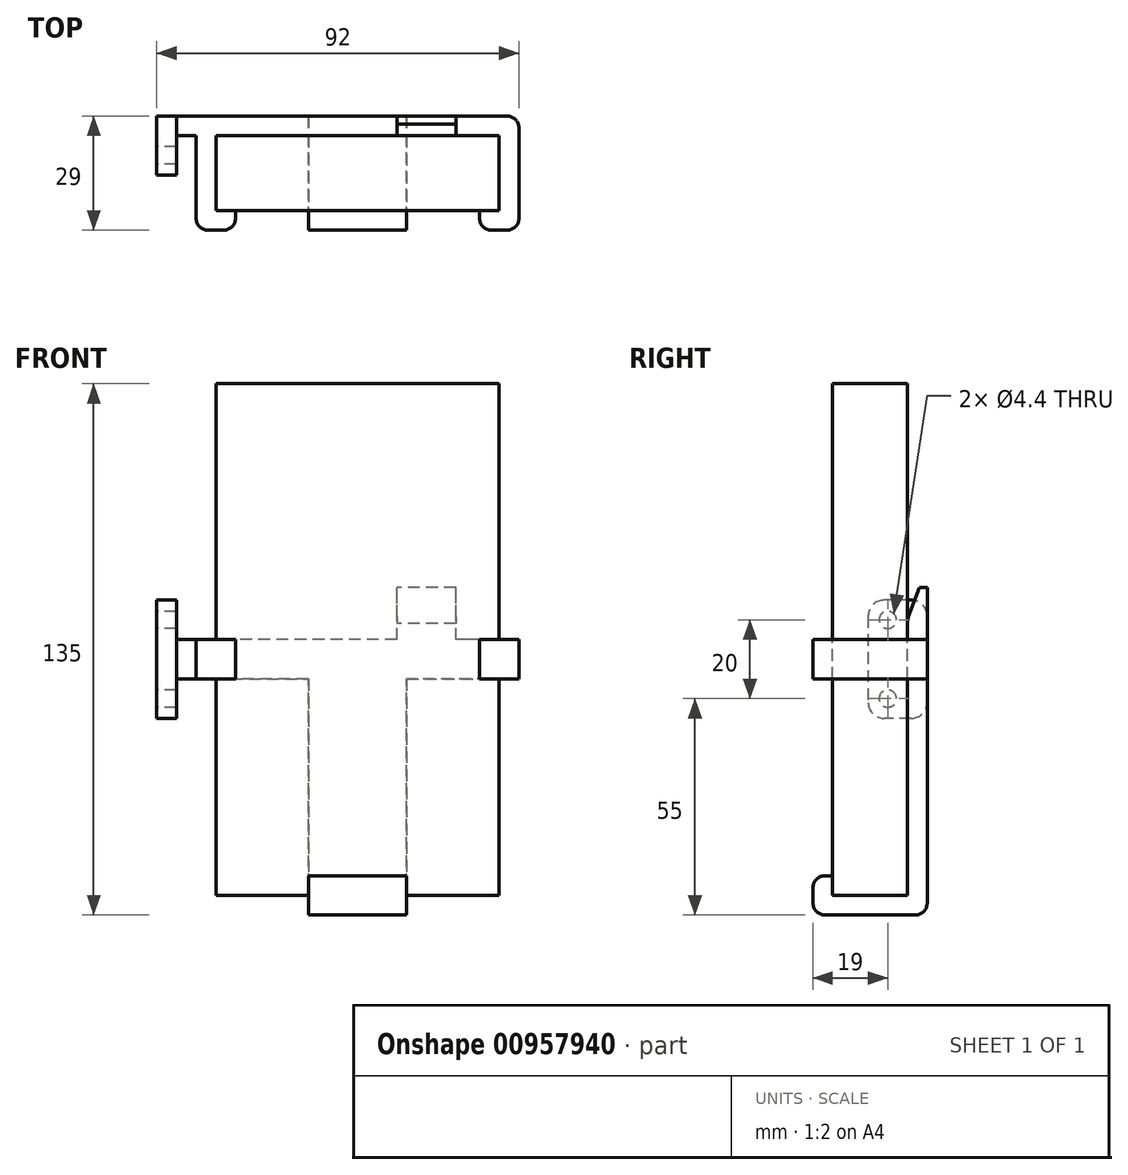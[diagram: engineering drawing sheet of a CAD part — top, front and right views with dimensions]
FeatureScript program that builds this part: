
annotation { "Feature Type Name" : "Feature", "Feature Type Description" : "" }
export const myFeature = defineFeature(function(context is Context, id is Id, definition is map)
    precondition{}
    {
        {
            var Q0;
            Q0=qCreatedBy(makeId("Front.planeOp"),FACE);
            var sketch = newSketch(context, id + "F0", { "sketchPlane" : qUnion([Q0])});
            skLineSegment(sketch, "E0.bottom", {"start": v(36, 65) * mm, "end": v(-36, 65) * mm});
            skLineSegment(sketch, "E0.top", {"start": v(36, -65) * mm, "end": v(-36, -65) * mm});
            skLineSegment(sketch, "E0.left", {"start": v(36, 65) * mm, "end": v(36, -65) * mm});
            skLineSegment(sketch, "E0.right", {"start": v(-36, 65) * mm, "end": v(-36, -65) * mm});
            skPoint(sketch, "E0.middle", {"position": v(0, 0) * mm});
            skSolve(sketch);
        }
        {
            var Q0;
            Q0=makeQuery(id+"F0.imprint","IMPRINT",FACE,{"disambiguationData":[TD([[makeQuery(id+"F0.imprint","IMPRINT",EDGE,{"derivedFrom":sQuery(id+"F0.wireOp",EDGE,"E0.bottom")}),1.0]])]});
            extrude(context, id + "F1", {"entities" : qUnion([Q0]), "depth" : 19 * mm, "offsetDistance" : 25 * mm});
        }
        {
            var Q0;
            Q0=qCreatedBy(makeId("Right.planeOp"),FACE);
            var sketch = newSketch(context, id + "F2", { "sketchPlane" : qUnion([Q0])});
            skLineSegment(sketch, "E1", {"start": v(0, 0) * mm, "end": v(0, -65) * mm});
            skLineSegment(sketch, "E2", {"start": v(0, -65) * mm, "end": v(-19, -65) * mm});
            skLineSegment(sketch, "E3", {"start": v(-19, -65) * mm, "end": v(-19, -60) * mm});
            skLineSegment(sketch, "E4", {"start": v(-19, -60) * mm, "end": v(-24, -60) * mm});
            skLineSegment(sketch, "E5", {"start": v(-24, -60) * mm, "end": v(-24, -70) * mm});
            skLineSegment(sketch, "E6", {"start": v(-24, -70) * mm, "end": v(5, -70) * mm});
            skLineSegment(sketch, "E7", {"start": v(5, -70) * mm, "end": v(5, 0) * mm});
            skLineSegment(sketch, "E8", {"start": v(5, 0) * mm, "end": v(0, 0) * mm});
            skLineSegment(sketch, "E9", {"start": v(0, -65) * mm, "end": v(0, 0) * mm});
            skSolve(sketch);
        }
        {
            var Q0;
            Q0=makeQuery(id+"F2.imprint","IMPRINT",FACE,{"disambiguationData":[TD([[makeQuery(id+"F2.imprint","IMPRINT",EDGE,{"derivedFrom":sQuery(id+"F2.wireOp",EDGE,"E2")}),1.0]])]});
            extrude(context, id + "F3", {"entities" : qUnion([Q0]), "endBound" : BoundingType.SYMMETRIC, "depth" : 25 * mm, "offsetDistance" : 25 * mm});
        }
        {
            var Q0;
            Q0=makeQuery(id+"F3.opExtrude","SWEPT_EDGE",EDGE,{"disambiguationData":[OSD([sQuery(id+"F2.wireOp",EDGE,"E4"),sQuery(id+"F2.wireOp",EDGE,"E5")])]});
            var Q1;
            Q1=makeQuery(id+"F3.opExtrude","SWEPT_EDGE",EDGE,{"disambiguationData":[OSD([sQuery(id+"F2.wireOp",EDGE,"E5"),sQuery(id+"F2.wireOp",EDGE,"E6")])]});
            var Q2;
            Q2=makeQuery(id+"F3.opExtrude","SWEPT_EDGE",EDGE,{"disambiguationData":[OSD([sQuery(id+"F2.wireOp",EDGE,"E6"),sQuery(id+"F2.wireOp",EDGE,"E7")])]});
            fillet(context, id + "F4", {"entities" : qUnion([Q0, Q1, Q2]), "radius" : 3 * mm, "tangentPropagation" : true, "allowEdgeOverflow" : false});
        }
        {
            var Q0;
            Q0=qCreatedBy(makeId("Top.planeOp"),FACE);
            var sketch = newSketch(context, id + "F5", { "sketchPlane" : qUnion([Q0])});
            skLineSegment(sketch, "E10", {"start": v(12.5, 0) * mm, "end": v(36, 0) * mm});
            skLineSegment(sketch, "E11", {"start": v(36, 0) * mm, "end": v(36, -19) * mm});
            skLineSegment(sketch, "E12", {"start": v(36, -19) * mm, "end": v(31, -19) * mm});
            skLineSegment(sketch, "E13", {"start": v(31, -19) * mm, "end": v(31, -24) * mm});
            skLineSegment(sketch, "E14", {"start": v(31, -24) * mm, "end": v(41, -24) * mm});
            skLineSegment(sketch, "E15", {"start": v(41, -24) * mm, "end": v(41, 5) * mm});
            skLineSegment(sketch, "E16", {"start": v(41, 5) * mm, "end": v(12.5, 5) * mm});
            skLineSegment(sketch, "E17", {"start": v(12.5, 5) * mm, "end": v(12.5, 0) * mm});
            skLineSegment(sketch, "E18.MirrorCS", {"start": v(-12.5, 5) * mm, "end": v(-12.5, 0) * mm});
            skLineSegment(sketch, "E19.MirrorCS", {"start": v(-12.5, 0) * mm, "end": v(-36, 0) * mm});
            skLineSegment(sketch, "E20.MirrorCS", {"start": v(-36, 0) * mm, "end": v(-36, -19) * mm});
            skLineSegment(sketch, "E21.MirrorCS", {"start": v(-36, -19) * mm, "end": v(-31, -19) * mm});
            skLineSegment(sketch, "E22.MirrorCS", {"start": v(-31, -19) * mm, "end": v(-31, -24) * mm});
            skLineSegment(sketch, "E23.MirrorCS", {"start": v(-31, -24) * mm, "end": v(-41, -24) * mm});
            skLineSegment(sketch, "E24.MirrorCS", {"start": v(-41, -24) * mm, "end": v(-41, 5) * mm});
            skLineSegment(sketch, "E25.MirrorCS", {"start": v(-41, 5) * mm, "end": v(-12.5, 5) * mm});
            skSolve(sketch);
        }
        {
            var Q0;
            Q0=makeQuery(id+"F5.imprint","IMPRINT",FACE,{"disambiguationData":[TD([[makeQuery(id+"F5.imprint","IMPRINT",EDGE,{"derivedFrom":sQuery(id+"F5.wireOp",EDGE,"E10")}),1.0]])]});
            var Q1;
            Q1=makeQuery(id+"F5.imprint","IMPRINT",FACE,{"disambiguationData":[TD([[makeQuery(id+"F5.imprint","IMPRINT",EDGE,{"derivedFrom":sQuery(id+"F5.wireOp",EDGE,"E18.MirrorCS")}),-1.0]])]});
            extrude(context, id + "F6", {"entities" : qUnion([Q0, Q1]), "operationType" : NewBodyOperationType.ADD, "oppositeDirection" : true, "depth" : 10 * mm, "offsetDistance" : 25 * mm});
        }
        {
            var Q0;
            Q0=makeQuery(id+"F6.opExtrude","SWEPT_EDGE",EDGE,{"disambiguationData":[OSD([sQuery(id+"F5.wireOp",EDGE,"E13"),sQuery(id+"F5.wireOp",EDGE,"E14")])]});
            var Q1;
            Q1=makeQuery(id+"F6.opExtrude","SWEPT_EDGE",EDGE,{"disambiguationData":[OSD([sQuery(id+"F5.wireOp",EDGE,"E14"),sQuery(id+"F5.wireOp",EDGE,"E15")])]});
            var Q2;
            Q2=makeQuery(id+"F6.opExtrude","SWEPT_EDGE",EDGE,{"disambiguationData":[OSD([sQuery(id+"F5.wireOp",EDGE,"E15"),sQuery(id+"F5.wireOp",EDGE,"E16")])]});
            var Q3;
            Q3=makeQuery(id+"F6.opExtrude","SWEPT_EDGE",EDGE,{"disambiguationData":[OSD([sQuery(id+"F5.wireOp",EDGE,"E23.MirrorCS"),sQuery(id+"F5.wireOp",EDGE,"E24.MirrorCS")])]});
            var Q4;
            Q4=makeQuery(id+"F6.opExtrude","SWEPT_EDGE",EDGE,{"disambiguationData":[OSD([sQuery(id+"F5.wireOp",EDGE,"E22.MirrorCS"),sQuery(id+"F5.wireOp",EDGE,"E23.MirrorCS")])]});
            fillet(context, id + "F7", {"entities" : qUnion([Q0, Q1, Q2, Q3, Q4]), "radius" : 3 * mm, "tangentPropagation" : true, "allowEdgeOverflow" : false});
        }
        {
            var Q0;
            Q0=qCreatedBy(makeId("Top.planeOp"),FACE);
            var sketch = newSketch(context, id + "F8", { "sketchPlane" : qUnion([Q0])});
            skPoint(sketch, "E26.0", {"position": v(-41, 5) * mm});
            skLineSegment(sketch, "E27.bottom", {"start": v(-41, 5) * mm, "end": v(-51, 5) * mm});
            skLineSegment(sketch, "E27.top", {"start": v(-41, 0) * mm, "end": v(-51, 0) * mm});
            skLineSegment(sketch, "E27.left", {"start": v(-41, 5) * mm, "end": v(-41, 0) * mm});
            skLineSegment(sketch, "E27.right", {"start": v(-51, 5) * mm, "end": v(-51, 0) * mm});
            skSolve(sketch);
        }
        {
            var Q0;
            Q0=makeQuery(id+"F8.imprint","IMPRINT",FACE,{"disambiguationData":[TD([[makeQuery(id+"F8.imprint","IMPRINT",EDGE,{"derivedFrom":sQuery(id+"F8.wireOp",EDGE,"E27.bottom")}),1.0]])]});
            var Q1;
            Q1=makeQuery(id+"F6.opExtrude","CAP_FACE",FACE,{"disambiguationData":[OSD([sQuery(id+"F5.wireOp",EDGE,"E18.MirrorCS"),sQuery(id+"F5.wireOp",EDGE,"E19.MirrorCS"),sQuery(id+"F5.wireOp",EDGE,"E20.MirrorCS"),sQuery(id+"F5.wireOp",EDGE,"E21.MirrorCS"),sQuery(id+"F5.wireOp",EDGE,"E22.MirrorCS"),sQuery(id+"F5.wireOp",EDGE,"E23.MirrorCS"),sQuery(id+"F5.wireOp",EDGE,"E24.MirrorCS"),sQuery(id+"F5.wireOp",EDGE,"E25.MirrorCS")])],"isStart":false});
            extrude(context, id + "F9", {"entities" : qUnion([Q0]), "operationType" : NewBodyOperationType.ADD, "endBound" : BoundingType.UP_TO_SURFACE, "oppositeDirection" : true, "depth" : 25 * mm, "endBoundEntityFace" : qUnion([Q1]), "offsetDistance" : 25 * mm});
        }
        {
            var Q0;
            Q0=makeQuery(id+"F9.opExtrude","SWEPT_FACE",FACE,{"disambiguationData":[OSD([sQuery(id+"F8.wireOp",EDGE,"E27.right")])]});
            var sketch = newSketch(context, id + "F10", { "sketchPlane" : qUnion([Q0])});
            skLineSegment(sketch, "E28.bottom", {"start": v(-5, 10) * mm, "end": v(10, 10) * mm});
            skLineSegment(sketch, "E28.top", {"start": v(-5, -20) * mm, "end": v(10, -20) * mm});
            skLineSegment(sketch, "E28.left", {"start": v(-5, 10) * mm, "end": v(-5, -20) * mm});
            skLineSegment(sketch, "E28.right", {"start": v(10, 10) * mm, "end": v(10, -20) * mm});
            skLineSegment(sketch, "E29", {"start": v(-5, -5) * mm, "end": v(28.25, -5) * mm, "construction": true});
            skCircle(sketch, "E30", {"center": v(5, 5) * mm, "radius": 2.2 * mm});
            skCircle(sketch, "E31.MirrorC", {"center": v(5, -15) * mm, "radius": 2.2 * mm});
            skLineSegment(sketch, "E32", {"start": v(5, -20) * mm, "end": v(5, 10) * mm, "construction": true});
            skSolve(sketch);
        }
        {
            var Q0;
            {var subQ5=sQuery(id+"F10.wireOp",EDGE,"E28.bottom");Q0=makeQuery(id+"F10.imprint","IMPRINT",FACE,{"disambiguationData":[TD([[makeQuery(id+"F10.imprint","IMPRINT",EDGE,{"derivedFrom":subQ5}),-1.0]])]});}
            extrude(context, id + "F11", {"entities" : qUnion([Q0]), "operationType" : NewBodyOperationType.ADD, "oppositeDirection" : true, "depth" : 5 * mm, "offsetDistance" : 25 * mm});
        }
        {
            var Q0;
            Q0=makeQuery(id+"F11.opExtrude","SWEPT_EDGE",EDGE,{"disambiguationData":[OSD([sQuery(id+"F10.wireOp",EDGE,"E28.bottom"),sQuery(id+"F10.wireOp",EDGE,"E28.right")])]});
            var Q1;
            Q1=makeQuery(id+"F11.opExtrude","SWEPT_EDGE",EDGE,{"disambiguationData":[OSD([sQuery(id+"F10.wireOp",EDGE,"E28.top"),sQuery(id+"F10.wireOp",EDGE,"E28.right")])]});
            var Q2;
            Q2=makeQuery(id+"F11.opExtrude","SWEPT_EDGE",EDGE,{"disambiguationData":[OSD([sQuery(id+"F10.wireOp",EDGE,"E28.bottom"),sQuery(id+"F10.wireOp",EDGE,"E28.left")])]});
            var Q3;
            Q3=makeQuery(id+"F11.opExtrude","SWEPT_EDGE",EDGE,{"disambiguationData":[OSD([sQuery(id+"F10.wireOp",EDGE,"E28.top"),sQuery(id+"F10.wireOp",EDGE,"E28.left")])]});
            fillet(context, id + "F12", {"entities" : qUnion([Q0, Q1, Q2, Q3]), "radius" : 4 * mm, "tangentPropagation" : true, "allowEdgeOverflow" : false});
        }
        {
            var Q0;
            Q0=qCreatedBy(makeId("Right.planeOp"),FACE);
            var sketch = newSketch(context, id + "F13", { "sketchPlane" : qUnion([Q0])});
            skLineSegment(sketch, "E33.bottom", {"start": v(0, 0) * mm, "end": v(5, 0) * mm});
            skLineSegment(sketch, "E33.top", {"start": v(3, 13.24) * mm, "end": v(5, 13.24) * mm});
            skLineSegment(sketch, "E33.right", {"start": v(5, 0) * mm, "end": v(5, 13.24) * mm});
            skLineSegment(sketch, "E34", {"start": v(0, 0) * mm, "end": v(0, 4.12) * mm});
            skLineSegment(sketch, "E35", {"start": v(0.3, 5.83) * mm, "end": v(3, 13.24) * mm});
            skPoint(sketch, "E36.visualSharp", {"position": v(0, 5) * mm});
            skArc(sketch, "E36.filletArc", {"start": v(0.3, 5.83) * mm, "mid": v(0.08, 4.99) * mm, "end": v(0, 4.12) * mm});
            skSolve(sketch);
        }
        {
            var Q0;
            Q0=makeQuery(id+"F13.imprint","IMPRINT",FACE,{"disambiguationData":[TD([[makeQuery(id+"F13.imprint","IMPRINT",EDGE,{"derivedFrom":sQuery(id+"F13.wireOp",EDGE,"E33.bottom")}),1.0]])]});
            extrude(context, id + "F14", {"entities" : qUnion([Q0]), "operationType" : NewBodyOperationType.ADD, "depth" : 25 * mm, "offsetDistance" : 25 * mm, "hasSecondDirection" : true, "secondDirectionOppositeDirection" : false, "secondDirectionDepth" : 10 * mm});
        }
    });
